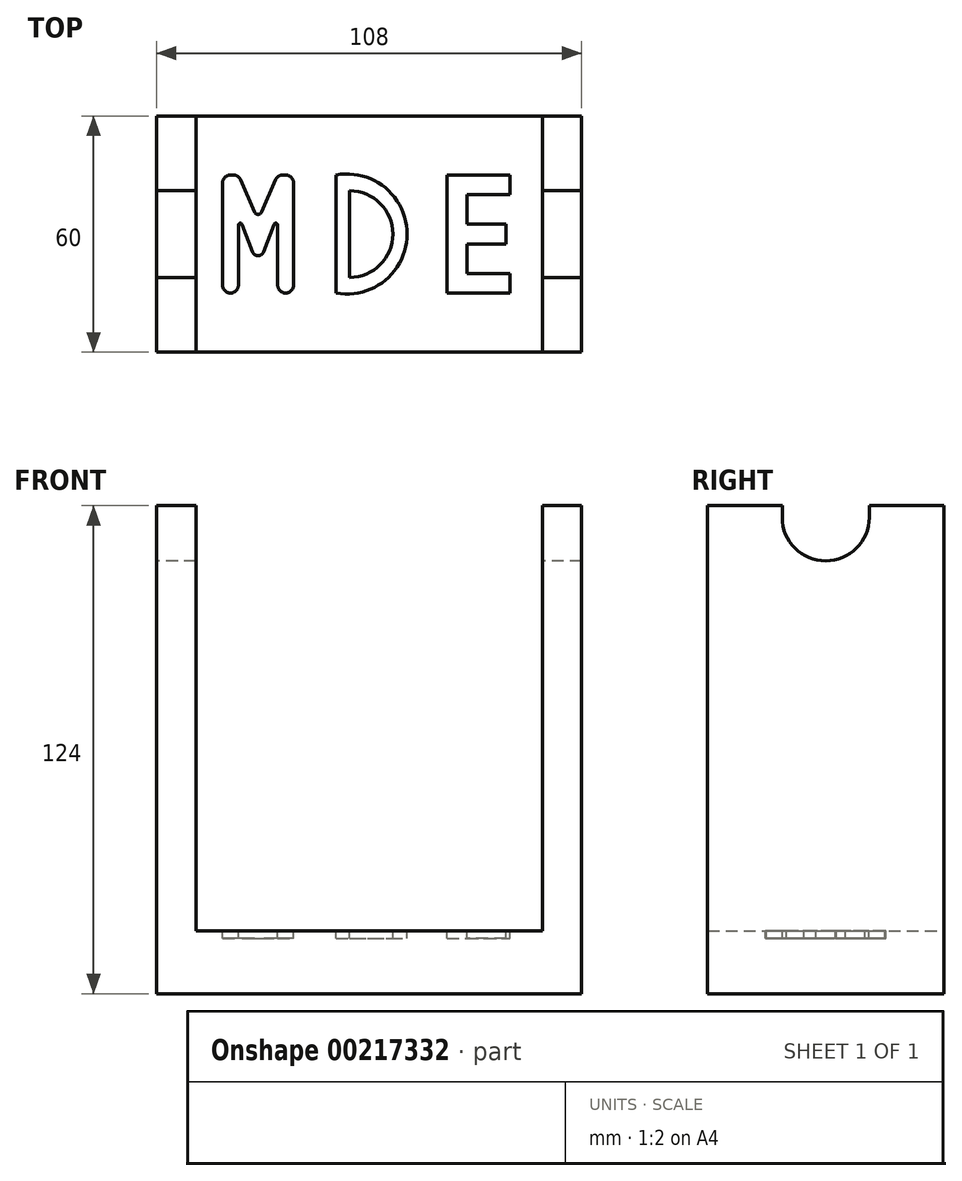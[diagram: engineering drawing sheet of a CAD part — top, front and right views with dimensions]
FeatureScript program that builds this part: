
annotation { "Feature Type Name" : "Feature", "Feature Type Description" : "" }
export const myFeature = defineFeature(function(context is Context, id is Id, definition is map)
    precondition{}
    {
        {
            var Q0;
            Q0=qCreatedBy(makeId("Front.planeOp"),FACE);
            var sketch = newSketch(context, id + "F0", { "sketchPlane" : qUnion([Q0])});
            skLineSegment(sketch, "E0.bottom", {"start": v(-54, -34.8) * mm, "end": v(54, -34.8) * mm});
            skLineSegment(sketch, "E0.top", {"start": v(-54, 89.2) * mm, "end": v(54, 89.2) * mm});
            skLineSegment(sketch, "E0.left", {"start": v(-54, -34.8) * mm, "end": v(-54, 89.2) * mm});
            skLineSegment(sketch, "E0.right", {"start": v(54, -34.8) * mm, "end": v(54, 89.2) * mm});
            skLineSegment(sketch, "E1.bottom", {"start": v(-44, 89.2) * mm, "end": v(44, 89.2) * mm});
            skLineSegment(sketch, "E1.top", {"start": v(-44, -18.8) * mm, "end": v(44, -18.8) * mm});
            skLineSegment(sketch, "E1.left", {"start": v(-44, 89.2) * mm, "end": v(-44, -18.8) * mm});
            skLineSegment(sketch, "E1.right", {"start": v(44, 89.2) * mm, "end": v(44, -18.8) * mm});
            skSolve(sketch);
        }
        {
            var Q0;
            Q0=makeQuery(id+"F0.imprint","IMPRINT",FACE,{"disambiguationData":[TD([[makeQuery(id+"F0.imprint","IMPRINT",EDGE,{"derivedFrom":sQuery(id+"F0.wireOp",EDGE,"E0.bottom")}),1.0]])]});
            extrude(context, id + "F1", {"entities" : qUnion([Q0]), "endBound" : BoundingType.SYMMETRIC, "depth" : 60 * mm});
        }
        {
            var Q0;
            Q0=qCreatedBy(makeId("Right.planeOp"),FACE);
            var sketch = newSketch(context, id + "F2", { "sketchPlane" : qUnion([Q0])});
            skArc(sketch, "E2", {"start": v(-11.05, 86.2) * mm, "mid": v(0, 75.15) * mm, "end": v(11.05, 86.2) * mm});
            skLineSegment(sketch, "E3", {"start": v(-11.05, 89.2) * mm, "end": v(-11.05, 86.2) * mm});
            skLineSegment(sketch, "E4", {"start": v(11.05, 89.2) * mm, "end": v(11.05, 86.2) * mm});
            skLineSegment(sketch, "E5", {"start": v(-11.05, 89.2) * mm, "end": v(11.05, 89.2) * mm});
            skSolve(sketch);
        }
        {
            var Q0;
            Q0 = qSketchRegion(id + "F2", true);
            extrude(context, id + "F3", {"entities" : qUnion([Q0]), "operationType" : NewBodyOperationType.REMOVE, "endBound" : BoundingType.SYMMETRIC, "depth" : 200 * mm});
        }
        {
            var Q0;
            Q0=makeQuery(id+"F1.opExtrude","SWEPT_FACE",FACE,{"disambiguationData":[OSD([sQuery(id+"F0.wireOp",EDGE,"E1.top")])]});
            var sketch = newSketch(context, id + "F4", { "sketchPlane" : qUnion([Q0])});
            skLineSegment(sketch, "E6.bottom", {"start": v(40.92, 26.59) * mm, "end": v(-40.92, 26.59) * mm, "construction": true});
            skLineSegment(sketch, "E6.top", {"start": v(40.92, -26.59) * mm, "end": v(-40.92, -26.59) * mm, "construction": true});
            skLineSegment(sketch, "E6.left", {"start": v(40.92, 26.59) * mm, "end": v(40.92, -26.59) * mm, "construction": true});
            skLineSegment(sketch, "E6.right", {"start": v(-40.92, 26.59) * mm, "end": v(-40.92, -26.59) * mm, "construction": true});
            skPoint(sketch, "E6.middle", {"position": v(0, 0) * mm});
            skLineSegment(sketch, "E7", {"start": v(-37.22, 13) * mm, "end": v(-37.22, -13) * mm});
            skLineSegment(sketch, "E8", {"start": v(-35.22, -15) * mm, "end": v(-35.22, -15) * mm});
            skLineSegment(sketch, "E9", {"start": v(-33.22, -13) * mm, "end": v(-33.22, 2.26) * mm});
            skLineSegment(sketch, "E10", {"start": v(-32.25, 2.44) * mm, "end": v(-29.62, -4.53) * mm});
            skLineSegment(sketch, "E11", {"start": v(-26.81, -4.53) * mm, "end": v(-24.18, 2.44) * mm});
            skLineSegment(sketch, "E12", {"start": v(-23.22, 2.26) * mm, "end": v(-23.22, -13) * mm});
            skLineSegment(sketch, "E13", {"start": v(-21.22, -15) * mm, "end": v(-21.22, -15) * mm});
            skLineSegment(sketch, "E14", {"start": v(-19.22, -13) * mm, "end": v(-19.22, 13) * mm});
            skLineSegment(sketch, "E15", {"start": v(-21.22, 15) * mm, "end": v(-21.9, 15) * mm});
            skLineSegment(sketch, "E16", {"start": v(-23.74, 13.8) * mm, "end": v(-27.3, 5.6) * mm});
            skLineSegment(sketch, "E17", {"start": v(-29.13, 5.6) * mm, "end": v(-32.7, 13.8) * mm});
            skLineSegment(sketch, "E18", {"start": v(-34.53, 15) * mm, "end": v(-35.22, 15) * mm});
            skPoint(sketch, "E19.visualSharp", {"position": v(-28.22, -8.25) * mm});
            skArc(sketch, "E19.filletArc", {"start": v(-29.62, -4.53) * mm, "mid": v(-28.22, -5.5) * mm, "end": v(-26.81, -4.53) * mm});
            skPoint(sketch, "E20.visualSharp", {"position": v(-28.22, 3.5) * mm});
            skArc(sketch, "E20.filletArc", {"start": v(-29.13, 5.6) * mm, "mid": v(-28.22, 5) * mm, "end": v(-27.3, 5.6) * mm});
            skPoint(sketch, "E21.visualSharp", {"position": v(-37.22, -15) * mm});
            skArc(sketch, "E21.filletArc", {"start": v(-37.22, -13) * mm, "mid": v(-36.63, -14.41) * mm, "end": v(-35.22, -15) * mm});
            skPoint(sketch, "E22.visualSharp", {"position": v(-33.22, -15) * mm});
            skArc(sketch, "E22.filletArc", {"start": v(-35.22, -15) * mm, "mid": v(-33.8, -14.41) * mm, "end": v(-33.22, -13) * mm});
            skPoint(sketch, "E23.visualSharp", {"position": v(-23.22, -15) * mm});
            skArc(sketch, "E23.filletArc", {"start": v(-23.22, -13) * mm, "mid": v(-22.63, -14.41) * mm, "end": v(-21.22, -15) * mm});
            skPoint(sketch, "E24.visualSharp", {"position": v(-19.22, -15) * mm});
            skArc(sketch, "E24.filletArc", {"start": v(-21.22, -15) * mm, "mid": v(-19.8, -14.41) * mm, "end": v(-19.22, -13) * mm});
            skPoint(sketch, "E25.newPointB", {"position": v(-37.22, 15) * mm});
            skArc(sketch, "E25.filletArc", {"start": v(-35.22, 15) * mm, "mid": v(-36.63, 14.41) * mm, "end": v(-37.22, 13) * mm});
            skPoint(sketch, "E26.visualSharp", {"position": v(-33.22, 15) * mm});
            skArc(sketch, "E26.filletArc", {"start": v(-32.7, 13.8) * mm, "mid": v(-33.43, 14.67) * mm, "end": v(-34.53, 15) * mm});
            skPoint(sketch, "E27.visualSharp", {"position": v(-23.22, 15) * mm});
            skArc(sketch, "E27.filletArc", {"start": v(-21.9, 15) * mm, "mid": v(-23, 14.67) * mm, "end": v(-23.74, 13.8) * mm});
            skPoint(sketch, "E28.visualSharp", {"position": v(-19.22, 15) * mm});
            skArc(sketch, "E28.filletArc", {"start": v(-19.22, 13) * mm, "mid": v(-19.8, 14.41) * mm, "end": v(-21.22, 15) * mm});
            skPoint(sketch, "E29.visualSharp", {"position": v(-33.22, 5) * mm});
            skArc(sketch, "E29.filletArc", {"start": v(-32.25, 2.44) * mm, "mid": v(-32.8, 2.75) * mm, "end": v(-33.22, 2.26) * mm});
            skPoint(sketch, "E30.visualSharp", {"position": v(-23.22, 5) * mm});
            skArc(sketch, "E30.filletArc", {"start": v(-23.22, 2.26) * mm, "mid": v(-23.63, 2.75) * mm, "end": v(-24.18, 2.44) * mm});
            skSolve(sketch);
        }
        {
            var Q0;
            Q0=makeQuery(id+"F4.imprint","IMPRINT",FACE,{"disambiguationData":[TD([[makeQuery(id+"F4.imprint","IMPRINT",EDGE,{"derivedFrom":sQuery(id+"F4.wireOp",EDGE,"E7")}),1.0]])]});
            extrude(context, id + "F5", {"entities" : qUnion([Q0]), "operationType" : NewBodyOperationType.REMOVE, "oppositeDirection" : true, "depth" : 2 * mm});
        }
        {
            var Q0;
            Q0=makeQuery(id+"F1.opExtrude","SWEPT_FACE",FACE,{"disambiguationData":[OSD([sQuery(id+"F0.wireOp",EDGE,"E1.top")])]});
            var sketch = newSketch(context, id + "F6", { "sketchPlane" : qUnion([Q0])});
            skLineSegment(sketch, "E31", {"start": v(-8.36, -15) * mm, "end": v(-8.36, 15) * mm});
            skPoint(sketch, "E31.startSnap0", {"position": v(-21.22, -15) * mm});
            skArc(sketch, "E32", {"start": v(-8.36, -15) * mm, "mid": v(9.64, 0) * mm, "end": v(-8.36, 15) * mm});
            skLineSegment(sketch, "E33", {"start": v(-4.96, 11) * mm, "end": v(-4.96, -11) * mm});
            skArc(sketch, "E34", {"start": v(-4.96, -11) * mm, "mid": v(6.04, 0) * mm, "end": v(-4.96, 11) * mm});
            skSolve(sketch);
        }
        {
            var Q0;
            Q0=makeQuery(id+"F6.imprint","IMPRINT",FACE,{"disambiguationData":[TD([[makeQuery(id+"F6.imprint","IMPRINT",EDGE,{"derivedFrom":sQuery(id+"F6.wireOp",EDGE,"E31")}),-1.0]])]});
            extrude(context, id + "F7", {"entities" : qUnion([Q0]), "operationType" : NewBodyOperationType.REMOVE, "oppositeDirection" : true, "depth" : 2 * mm});
        }
        {
            var Q0;
            {var subQ1=sQuery(id+"F0.wireOp",EDGE,"E1.left");var subQ2=sQuery(id+"F0.wireOp",EDGE,"E1.top");Q0=makeQuery(id+"F7.boolean.opBoolean","SPLIT",FACE,{"disambiguationData":[TD([makeQuery(id+"F1.opExtrude","SWEPT_FACE",FACE,{"disambiguationData":[OSD([subQ1])]})])],"derivedFrom":makeQuery(id+"F1.opExtrude","SWEPT_FACE",FACE,{"disambiguationData":[OSD([subQ2])]})});}
            var sketch = newSketch(context, id + "F8", { "sketchPlane" : qUnion([Q0])});
            skLineSegment(sketch, "E35", {"start": v(19.82, -15) * mm, "end": v(19.82, 15) * mm});
            skLineSegment(sketch, "E36", {"start": v(19.82, 15) * mm, "end": v(35.82, 15) * mm});
            skLineSegment(sketch, "E37", {"start": v(35.82, 15) * mm, "end": v(35.82, 10) * mm});
            skLineSegment(sketch, "E38", {"start": v(35.82, 10) * mm, "end": v(24.82, 10) * mm});
            skLineSegment(sketch, "E39", {"start": v(24.82, 10) * mm, "end": v(24.82, 2.5) * mm});
            skLineSegment(sketch, "E40", {"start": v(24.82, 2.5) * mm, "end": v(34.82, 2.5) * mm});
            skLineSegment(sketch, "E41", {"start": v(34.82, 2.5) * mm, "end": v(34.82, -2.5) * mm});
            skLineSegment(sketch, "E42", {"start": v(34.82, -2.5) * mm, "end": v(24.82, -2.5) * mm});
            skLineSegment(sketch, "E43", {"start": v(24.82, -2.5) * mm, "end": v(24.82, -10) * mm});
            skLineSegment(sketch, "E44", {"start": v(24.82, -10) * mm, "end": v(35.82, -10) * mm});
            skLineSegment(sketch, "E45", {"start": v(35.82, -10) * mm, "end": v(35.82, -15) * mm});
            skLineSegment(sketch, "E46", {"start": v(19.82, -15) * mm, "end": v(35.82, -15) * mm});
            skPoint(sketch, "E47.orphan", {"position": v(35.82, -15.73) * mm});
            skSolve(sketch);
        }
        {
            var Q0;
            Q0 = qSketchRegion(id + "F8", true);
            extrude(context, id + "F9", {"entities" : qUnion([Q0]), "operationType" : NewBodyOperationType.REMOVE, "oppositeDirection" : true, "depth" : 2 * mm});
        }
    });
